# Revit family: Differential Pressure Control Valve 4002 45-80kPa
name_source: partatom
category: Rohrzubehör
revit_build: Autodesk Revit 2018 (Build: 20190510_1515(x64)
units: mm (PartAtom-declared; Revit-internal decimal feet)

## family parameters
Arbeitsebenenbasiert = Nein
Beim Laden mit Abzugskörper schneiden = Nein
Bemaßung runder Anschluss = Durchmesser verwenden
Gemeinsam genutzt = Nein
Immer vertikal = Ja
OmniClass-Nummer = 23.65.55.14
OmniClass-Titel = Valves for Liquid Services
Teiletyp = Unterbricht

## types (2) — shared parameters
Adjusting spindle = brass CW614N
Application = Differential pressure controllers are used to stabilize the differential pressure in heating and cooling circuits and ensure the
independence of the loads from dynamic pressure fluctuations in the system.
B01 = 10 mm  [stored 0.0328084 ft]
B02 = 104.688 mm  [stored 0.343465 ft]
B03 = 44.5 mm  [stored 0.145997 ft]
B04 = 100.649 mm  [stored 0.330213 ft]
Body = DZR brass CC770S
Compression spring = spring steel 14310 NS
Connection nipple = brass CW602N
Control range = 45 - 80kPa
H03 = 9.8 mm  [stored 0.0321522 ft]
H04 = 4 mm  [stored 0.0131234 ft]
Hersteller = HERZ-Armaturen Ges.m.b.H
Indicator sleeve = plastic (red)
Insulation shell = EPP (expanded polypropylen)
J1 = 6.5 mm
J10 = 18.897 mm  [stored 0.061998 ft]
J11 = 3.5 mm  [stored 0.0114829 ft]
J2 = 11 mm  [stored 0.0360892 ft]
J3 = 3.2 mm  [stored 0.0104987 ft]
J4 = 1.5 mm  [stored 0.00492126 ft]
J5 = 6.5 mm
J6 = 3.9 mm  [stored 0.0127953 ft]
J7 = 15.897 mm
J8 = 7.85 mm  [stored 0.0257546 ft]
J9 = 15.7 mm  [stored 0.0515092 ft]
K1 = 6.651 mm  [stored 0.0218209 ft]
K1.1 = 2.35 mm  [stored 0.00770997 ft]
K10 = 18.25 mm  [stored 0.0598753 ft]
K11 = 35 mm  [stored 0.114829 ft]
K12 = 10 mm  [stored 0.0328084 ft]
K13 = 16.649 mm  [stored 0.0546227 ft]
K14 = 16.649 mm  [stored 0.0546227 ft]
K15 = 26.649 mm  [stored 0.0874311 ft]
K16 = 3 mm  [stored 0.00984252 ft]
K17 = 66.7 mm  [stored 0.218832 ft]
K18 = 89 mm  [stored 0.291995 ft]
K2 = 2.35 mm  [stored 0.00770997 ft]
K3 = 15 mm  [stored 0.0492126 ft]
K4 = 12 mm  [stored 0.0393701 ft]
K5 = 13 mm
K6 = 11.7 mm  [stored 0.0383858 ft]
K7 = 8.7 mm  [stored 0.0285433 ft]
K8 = 55 mm  [stored 0.180446 ft]
K9 = 4 mm  [stored 0.0131234 ft]
L06 = 7 mm  [stored 0.0229659 ft]
Max. differential pressure on the body = 400000.0 Pa
Max. operating pressure = 1600000.0 Pa
Max. operating temperature from DN40 = 110 °C
Max. operating temperature up to DN32 = 130 °C
Membrane = EPDM
Membrane body = brass CW602N
Min. operating temperature (anti freeze) = -20 °C
Min. operating temperature (pure water) = 2 °C
Model = The differential pressure controller is a straight-version linear controller and works without auxiliary power. The
nominal differential pressure can be continuously adjusted from 450 to 800 mbar.
The value for the setting can be read from the diagram. The nominal set point is factory preset to a minimum. If
necessary, the nominal set point can be adjusted using the pre-setting key (1 4002 01). A capillary tube (1000 mm) is
included and should be connected to the circuit regulating valve in the supply line.
O-Rings = EPDM
R02 = 14.5 mm  [stored 0.0475722 ft]
Regulator connection nut = brass CW614N
S07 = 10 mm  [stored 0.0328084 ft]
SCRNCODE = 05;03;4
SCRNSEQ = ARM;ARM_TYP="DIFR";2
URL = www.herzvalves.com
V10 = 16 mm  [stored 0.0524934 ft]
V12 = 17 mm
Valve shaft = stainless steel 14301

## per-type parameters (varying)
| type | Dämmung | Materials | Medium |
| with insulation | Ja | EPDM gaskets can be affected by Mineral oils lubricants and thus lead to failure of the EPDM seals. Please refer
to manufacturers documentation when using ethylene glycol products for frost and corrosion protection | Water purity in accordance with the ÖNORM H 5195 and VDI 2035 standards
Ethylene and propylene glycol can be mixed to a ratio of 25 - 50 vol. [%] |
| without insulation | Nein | EPDM gaskets can be affected by mineral oil lubricants and thus lead to failure of the EPDM seals. Please refer
to manufacturers documentation when using ethylene glycol products for frost and corrosion protection. | Water purity in accordance with the ÖNORM H 5195 and VDI 2035 standards.
Ethylene and propylene glycol can be mixed to a ratio of 25 - 50 vol. [%] |

note: [stored X ft] marks values corroborated as IEEE doubles in the binary element streams (Revit-internal decimal feet)
